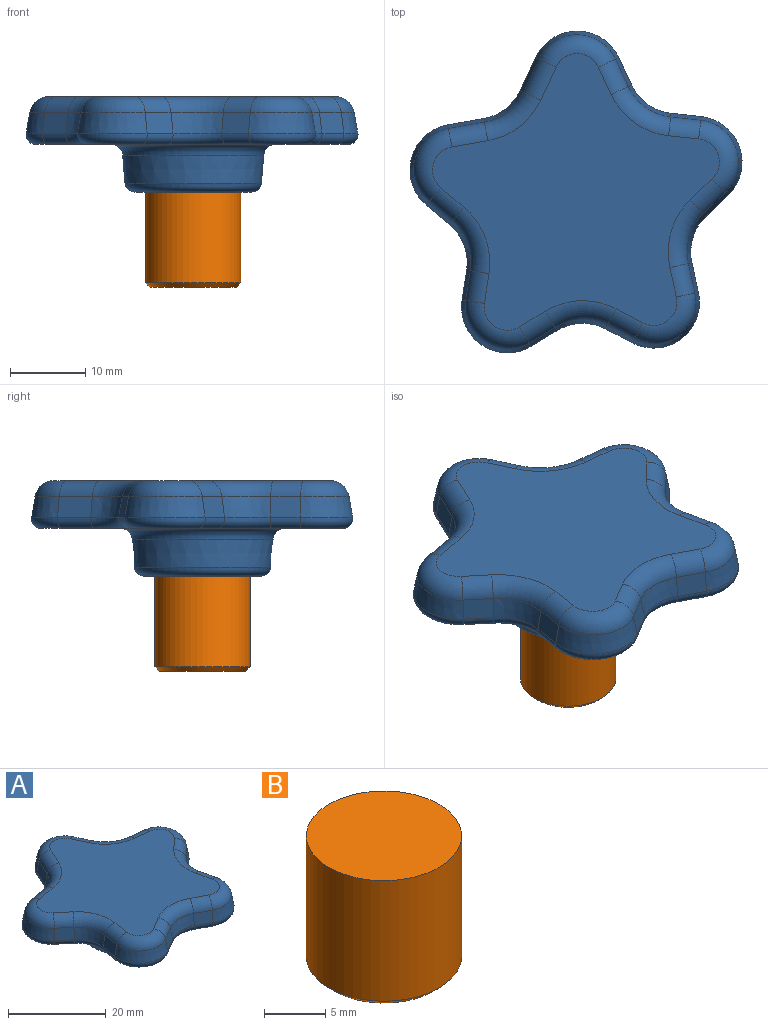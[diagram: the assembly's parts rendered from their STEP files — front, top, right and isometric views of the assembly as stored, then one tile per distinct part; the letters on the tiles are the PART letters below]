
ASSEMBLY  parts=2 mates=1
PART A: 66 faces, bbox 45.2x43.9x12.7 mm
  f0: cone r=6.35mm half-angle=10deg, axis (0,0,-1), area 37.2mm2, adj f1,f19,f37,f57
  f1: plane 4.62x2.76mm, normal (-0.89,0.42,0.17), area 13.6mm2, adj f0,f2,f35,f55
  f2: cone r=6.35mm half-angle=10deg, axis (0,0,1), area 18.4mm2, adj f1,f3,f33,f53
  f3: plane 4.88x2.76mm, normal (-0.17,0.97,0.17), area 13.6mm2, adj f2,f4,f31,f51
  f4: cone r=6.35mm half-angle=10deg, axis (0,0,-1), area 37.2mm2, adj f3,f5,f29,f49
  f5: plane 3.4x2.96mm, normal (-0.63,-0.75,0.17), area 11.3mm2, adj f4,f6,f27,f47
  f6: cone r=6.35mm half-angle=10deg, axis (0,0,1), area 19.7mm2, adj f5,f7,f25,f45
  f7: plane 4.06x2.76mm, normal (-0.97,0.15,0.17), area 11.3mm2, adj f6,f8,f23,f43
  f8: cone r=6.35mm half-angle=10deg, axis (0,0,-1), area 37.2mm2, adj f7,f9,f22,f42
  f9: plane 3.7x2.76mm, normal (0.51,-0.84,0.17), area 11.3mm2, adj f8,f10,f24,f44
  f10: cone r=6.35mm half-angle=10deg, axis (0,0,1), area 19.7mm2, adj f9,f11,f26,f46
  f11: plane 3.8x2.76mm, normal (-0.45,-0.87,0.17), area 11.3mm2, adj f10,f12,f28,f48
  f12: cone r=6.35mm half-angle=10deg, axis (0,0,-1), area 37.2mm2, adj f11,f13,f30,f50
  f13: plane 4.04x2.76mm, normal (0.96,0.21,0.17), area 11.3mm2, adj f12,f14,f32,f52
  f14: cone r=6.35mm half-angle=10deg, axis (0,0,1), area 19.7mm2, adj f13,f15,f34,f54
  f15: plane 3.25x3.14mm, normal (0.68,-0.71,0.17), area 11.3mm2, adj f14,f16,f36,f56
  f16: cone r=6.35mm half-angle=10deg, axis (0,0,-1), area 37.2mm2, adj f15,f17,f38,f58
  f17: plane 4.06x2.76mm, normal (0.11,0.98,0.17), area 11.3mm2, adj f16,f18,f40,f60
  f18: cone r=6.35mm half-angle=10deg, axis (0,0,1), area 19.7mm2, adj f17,f19,f41,f61
  f19: plane 3.86x2.76mm, normal (0.89,0.42,0.17), area 11.3mm2, adj f0,f18,f39,f59
  f20: plane 38.19x36.83mm, normal (0,0,1), area 795.6mm2, adj f22,f23,f24,f25,f26,f27,f28,f29
  f21: plane 41.66x40.3mm, normal (0,0,-1), area 644.8mm2, adj f42,f43,f44,f45,f46,f47,f48,f49
  f22: torus R=3.1mm, axis (0,0,1), area 37mm2, adj f8,f20,f23,f24
  f23: cylinder r=2.54mm len=4.36mm, axis (0.15,0.99,0), area 14.3mm2, adj f7,f20,f22,f25
  f24: cylinder r=2.54mm len=4.74mm, axis (0.85,0.52,0), area 14.3mm2, adj f9,f20,f22,f26
  f25: torus R=9.6mm, axis (0,0,1), area 29.4mm2, adj f6,f20,f23,f27
  f26: torus R=9.6mm, axis (0,0,1), area 29.4mm2, adj f10,f20,f24,f28
  f27: cylinder r=2.54mm len=4.7mm, axis (0.77,-0.64,0), area 14.3mm2, adj f5,f20,f25,f29
  f28: cylinder r=2.54mm len=4.73mm, axis (-0.89,0.46,0), area 14.3mm2, adj f11,f20,f26,f30
  f29: torus R=3.1mm, axis (0,0,1), area 37mm2, adj f4,f20,f27,f31
  f30: torus R=3.1mm, axis (0,0,1), area 37mm2, adj f12,f20,f28,f32
  f31: cylinder r=2.54mm len=5.23mm, axis (0.98,0.17,0), area 17.3mm2, adj f3,f20,f29,f33
  f32: cylinder r=2.54mm len=4.48mm, axis (-0.22,0.98,0), area 14.3mm2, adj f13,f20,f30,f34
  f33: torus R=9.6mm, axis (0,0,1), area 27.6mm2, adj f2,f20,f31,f35
  f34: torus R=9.6mm, axis (0,0,1), area 29.4mm2, adj f14,f20,f32,f36
  f35: cylinder r=2.54mm len=5.47mm, axis (-0.42,-0.91,0), area 17.3mm2, adj f1,f20,f33,f37
  f36: cylinder r=2.54mm len=4.64mm, axis (-0.72,-0.69,0), area 14.3mm2, adj f15,f20,f34,f38
  f37: torus R=3.1mm, axis (0,0,1), area 37mm2, adj f0,f20,f35,f39
  f38: torus R=3.1mm, axis (0,0,1), area 37mm2, adj f16,f20,f36,f40
  f39: cylinder r=2.54mm len=4.71mm, axis (0.42,-0.91,0), area 14.3mm2, adj f19,f20,f37,f41
  f40: cylinder r=2.54mm len=4.28mm, axis (-0.99,0.11,0), area 14.3mm2, adj f17,f20,f38,f41
  f41: torus R=9.6mm, axis (0,0,1), area 29.4mm2, adj f18,f20,f39,f40
  f42: torus R=4.84mm, axis (0,0,1), area 28.6mm2, adj f8,f21,f43,f44
  f43: cylinder r=1.27mm len=4.18mm, axis (-0.15,-0.99,0), area 8.9mm2, adj f7,f21,f42,f45
  f44: cylinder r=1.27mm len=4.1mm, axis (-0.85,-0.52,0), area 8.9mm2, adj f9,f21,f42,f46
  f45: torus R=7.86mm, axis (0,0,1), area 15.9mm2, adj f6,f21,f43,f47
  f46: torus R=7.86mm, axis (0,0,1), area 15.9mm2, adj f10,f21,f44,f48
  f47: cylinder r=1.27mm len=3.9mm, axis (-0.77,0.64,0), area 8.9mm2, adj f5,f21,f45,f49
  f48: cylinder r=1.27mm len=4.16mm, axis (0.89,-0.46,0), area 8.9mm2, adj f11,f21,f46,f50
  f49: torus R=4.84mm, axis (0,0,1), area 28.6mm2, adj f4,f21,f47,f51
  f50: torus R=4.84mm, axis (0,0,1), area 28.6mm2, adj f12,f21,f48,f52
  f51: cylinder r=1.27mm len=5.01mm, axis (-0.98,-0.17,0), area 10.8mm2, adj f3,f21,f49,f53
  f52: cylinder r=1.27mm len=4.21mm, axis (0.22,-0.98,0), area 8.9mm2, adj f13,f21,f50,f54
  f53: torus R=7.86mm, axis (0,0,1), area 14.9mm2, adj f2,f21,f51,f55
  f54: torus R=7.86mm, axis (0,0,1), area 15.9mm2, adj f14,f21,f52,f56
  f55: cylinder r=1.27mm len=4.95mm, axis (0.42,0.91,0), area 10.8mm2, adj f1,f21,f53,f57
  f56: cylinder r=1.27mm len=3.79mm, axis (0.72,0.69,0), area 8.9mm2, adj f15,f21,f54,f58
  f57: torus R=4.84mm, axis (0,0,1), area 28.6mm2, adj f0,f21,f55,f59
  f58: torus R=4.84mm, axis (0,0,1), area 28.6mm2, adj f16,f21,f56,f60
  f59: cylinder r=1.27mm len=4.19mm, axis (-0.42,0.91,0), area 8.9mm2, adj f19,f21,f57,f61
  f60: cylinder r=1.27mm len=4.14mm, axis (0.99,-0.11,0), area 8.9mm2, adj f17,f21,f58,f61
  f61: torus R=7.86mm, axis (0,0,1), area 15.9mm2, adj f18,f21,f59,f60
  f62: cone r=9.53mm half-angle=5deg, axis (0,0,1), area 217.9mm2, adj f64,f65
  f63: plane 15.61x15.61mm, normal (0,0,-1), area 191.4mm2, adj f65
  f64: torus R=10.98mm, axis (0,0,1), area 148mm2, adj f21,f62
  f65: torus R=7.81mm, axis (0,0,-1), area 101.7mm2, adj f62,f63
PART B: 4 faces, bbox 12.7x12.7x12.7 mm
  f0: cylinder r=6.35mm len=12.7mm, axis (0,0,1), area 481.4mm2, adj f2,f3
  f1: plane 11.43x11.43mm, normal (0,0,-1), area 102.6mm2, adj f3
  f2: plane 12.7x12.7mm, normal (0,0,1), area 126.7mm2, adj f0
  f3: cone r=5.71mm half-angle=45deg, axis (0,0,1), area 34mm2, adj f0,f1
PLACE A t=(-5.43,-986.24,-345.99)mm
PLACE B t=(-5.43,-986.24,-345.99)mm
MATE fastened B.f0 <-> A.f62  axis (0,0,1) through (-5.43,-986.24,-352.34)mm
